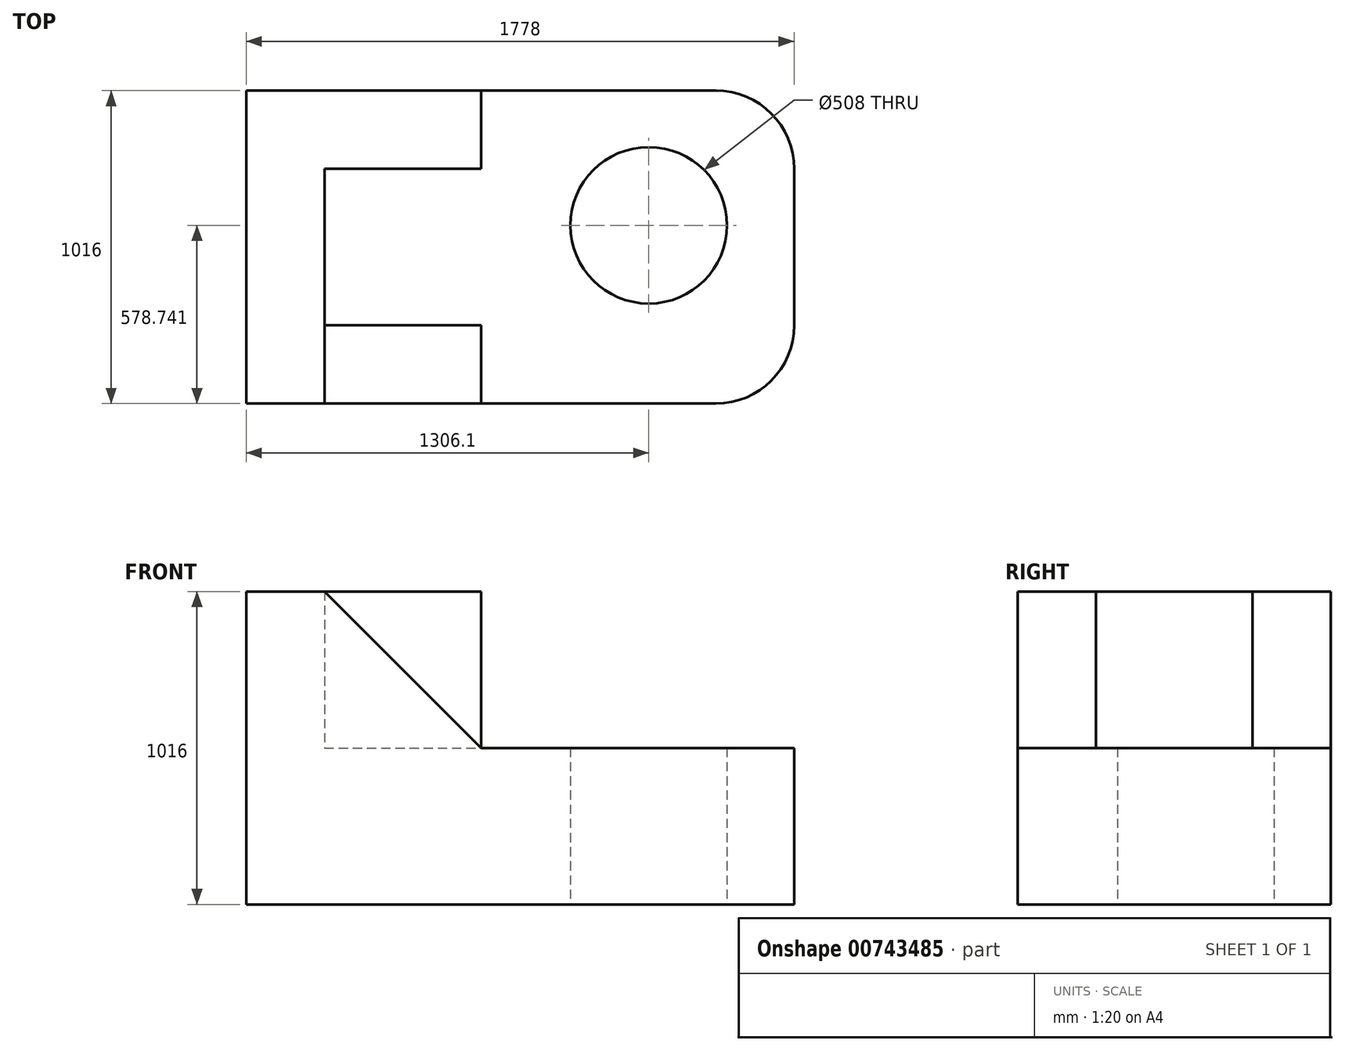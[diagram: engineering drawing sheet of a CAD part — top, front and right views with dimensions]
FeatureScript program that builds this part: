
annotation { "Feature Type Name" : "Feature", "Feature Type Description" : "" }
export const myFeature = defineFeature(function(context is Context, id is Id, definition is map)
    precondition{}
    {
        {
            var Q0;
            Q0=qCreatedBy(makeId("Top.planeOp"),FACE);
            var sketch = newSketch(context, id + "F0", { "sketchPlane" : qUnion([Q0])});
            skLineSegment(sketch, "E0.bottom", {"start": v(-1718.28, 975.56) * mm, "end": v(59.72, 975.56) * mm});
            skLineSegment(sketch, "E0.top", {"start": v(-1718.28, -40.44) * mm, "end": v(59.72, -40.44) * mm});
            skLineSegment(sketch, "E0.left", {"start": v(-1718.28, 975.56) * mm, "end": v(-1718.28, -40.44) * mm});
            skLineSegment(sketch, "E0.right", {"start": v(59.72, 975.56) * mm, "end": v(59.72, -40.44) * mm});
            skCircle(sketch, "E1", {"center": v(-412.18, 538.3) * mm, "radius": 254 * mm});
            skSolve(sketch);
        }
        {
            var Q0;
            Q0 = qSketchRegion(id + "F0", true);
            extrude(context, id + "F1", {"entities" : qUnion([Q0]), "depth" : 508 * mm, "offsetDistance" : 25.4 * mm});
        }
        {
            var Q0;
            Q0=makeQuery(id+"F1.opExtrude","SWEPT_EDGE",EDGE,{"disambiguationData":[OSD([sQuery(id+"F0.wireOp",EDGE,"E0.top"),sQuery(id+"F0.wireOp",EDGE,"E0.right")])]});
            var Q1;
            Q1=makeQuery(id+"F1.opExtrude","SWEPT_EDGE",EDGE,{"disambiguationData":[OSD([sQuery(id+"F0.wireOp",EDGE,"E0.bottom"),sQuery(id+"F0.wireOp",EDGE,"E0.right")])]});
            fillet(context, id + "F2", {"entities" : qUnion([Q0, Q1]), "radius" : 254 * mm, "tangentPropagation" : true, "allowEdgeOverflow" : false});
        }
        {
            var Q0;
            Q0=makeQuery(id+"F1.opExtrude","CAP_FACE",FACE,{"disambiguationData":[OSD([sQuery(id+"F0.wireOp",EDGE,"E0.bottom"),sQuery(id+"F0.wireOp",EDGE,"E0.top"),sQuery(id+"F0.wireOp",EDGE,"E0.left"),sQuery(id+"F0.wireOp",EDGE,"E0.right"),sQuery(id+"F0.wireOp",EDGE,"E1")])],"isStart":false});
            var sketch = newSketch(context, id + "F3", { "sketchPlane" : qUnion([Q0])});
            skLineSegment(sketch, "E2.bottom", {"start": v(-1718.28, 975.56) * mm, "end": v(-1464.28, 975.56) * mm});
            skLineSegment(sketch, "E2.top", {"start": v(-1718.28, -40.44) * mm, "end": v(-1464.28, -40.44) * mm});
            skLineSegment(sketch, "E2.left", {"start": v(-1718.28, 975.56) * mm, "end": v(-1718.28, -40.44) * mm});
            skLineSegment(sketch, "E2.right", {"start": v(-1464.28, 975.56) * mm, "end": v(-1464.28, -40.44) * mm});
            skSolve(sketch);
        }
        {
            var Q0;
            Q0 = qSketchRegion(id + "F3", true);
            extrude(context, id + "F4", {"entities" : qUnion([Q0]), "operationType" : NewBodyOperationType.ADD, "depth" : 508 * mm, "offsetDistance" : 25.4 * mm});
        }
        {
            var Q0;
            Q0=makeQuery(id+"F1.opExtrude","CAP_FACE",FACE,{"disambiguationData":[OSD([sQuery(id+"F0.wireOp",EDGE,"E0.bottom"),sQuery(id+"F0.wireOp",EDGE,"E0.top"),sQuery(id+"F0.wireOp",EDGE,"E0.left"),sQuery(id+"F0.wireOp",EDGE,"E0.right"),sQuery(id+"F0.wireOp",EDGE,"E1")])],"isStart":false});
            var sketch = newSketch(context, id + "F5", { "sketchPlane" : qUnion([Q0])});
            skLineSegment(sketch, "E3.bottom", {"start": v(-1464.28, 975.56) * mm, "end": v(-956.28, 975.56) * mm});
            skLineSegment(sketch, "E3.top", {"start": v(-1464.28, 721.56) * mm, "end": v(-956.28, 721.56) * mm});
            skLineSegment(sketch, "E3.left", {"start": v(-1464.28, 975.56) * mm, "end": v(-1464.28, 721.56) * mm});
            skLineSegment(sketch, "E3.right", {"start": v(-956.28, 975.56) * mm, "end": v(-956.28, 721.56) * mm});
            skSolve(sketch);
        }
        {
            var Q0;
            Q0 = qSketchRegion(id + "F5", true);
            extrude(context, id + "F6", {"entities" : qUnion([Q0]), "operationType" : NewBodyOperationType.ADD, "depth" : 508 * mm, "offsetDistance" : 25.4 * mm});
        }
        {
            var Q0;
            Q0=makeQuery(id+"F1.opExtrude","CAP_FACE",FACE,{"disambiguationData":[OSD([sQuery(id+"F0.wireOp",EDGE,"E0.bottom"),sQuery(id+"F0.wireOp",EDGE,"E0.top"),sQuery(id+"F0.wireOp",EDGE,"E0.left"),sQuery(id+"F0.wireOp",EDGE,"E0.right"),sQuery(id+"F0.wireOp",EDGE,"E1")])],"isStart":false});
            var sketch = newSketch(context, id + "F7", { "sketchPlane" : qUnion([Q0])});
            skLineSegment(sketch, "E4.bottom", {"start": v(-1464.28, 213.56) * mm, "end": v(-956.28, 213.56) * mm});
            skLineSegment(sketch, "E4.top", {"start": v(-1464.28, -40.44) * mm, "end": v(-956.28, -40.44) * mm});
            skLineSegment(sketch, "E4.left", {"start": v(-1464.28, 213.56) * mm, "end": v(-1464.28, -40.44) * mm});
            skLineSegment(sketch, "E4.right", {"start": v(-956.28, 213.56) * mm, "end": v(-956.28, -40.44) * mm});
            skSolve(sketch);
        }
        {
            var Q0;
            Q0 = qSketchRegion(id + "F7", true);
            extrude(context, id + "F8", {"entities" : qUnion([Q0]), "operationType" : NewBodyOperationType.ADD, "depth" : 508 * mm, "offsetDistance" : 25.4 * mm});
        }
        {
            var Q0;
            Q0=makeQuery(id+"F8.boolean.opBoolean","MERGE",FACE,{"derivedFrom":[makeQuery(id+"F4.boolean.opBoolean","MERGE",FACE,{"derivedFrom":[makeQuery(id+"F1.opExtrude","SWEPT_FACE",FACE,{"disambiguationData":[OSD([sQuery(id+"F0.wireOp",EDGE,"E0.top")])]}),makeQuery(id+"F4.opExtrude","SWEPT_FACE",FACE,{"disambiguationData":[OSD([sQuery(id+"F3.wireOp",EDGE,"E2.top")])]})]}),makeQuery(id+"F8.opExtrude","SWEPT_FACE",FACE,{"disambiguationData":[OSD([sQuery(id+"F7.wireOp",EDGE,"E4.top")])]})]});
            var sketch = newSketch(context, id + "F9", { "sketchPlane" : qUnion([Q0])});
            skLineSegment(sketch, "E5", {"start": v(-956.28, 508) * mm, "end": v(-956.28, 1016) * mm});
            skLineSegment(sketch, "E6", {"start": v(-956.28, 1016) * mm, "end": v(-1464.28, 1016) * mm});
            skLineSegment(sketch, "E7", {"start": v(-1464.28, 1016) * mm, "end": v(-956.28, 508) * mm});
            skSolve(sketch);
        }
        {
            var Q0;
            Q0=makeQuery(id+"F9.imprint","IMPRINT",FACE,{"disambiguationData":[TD([[makeQuery(id+"F9.imprint","IMPRINT",EDGE,{"derivedFrom":sQuery(id+"F9.wireOp",EDGE,"E5")}),-1.0]])]});
            extrude(context, id + "F10", {"entities" : qUnion([Q0]), "operationType" : NewBodyOperationType.REMOVE, "oppositeDirection" : true, "depth" : 254 * mm, "offsetDistance" : 25.4 * mm});
        }
    });
